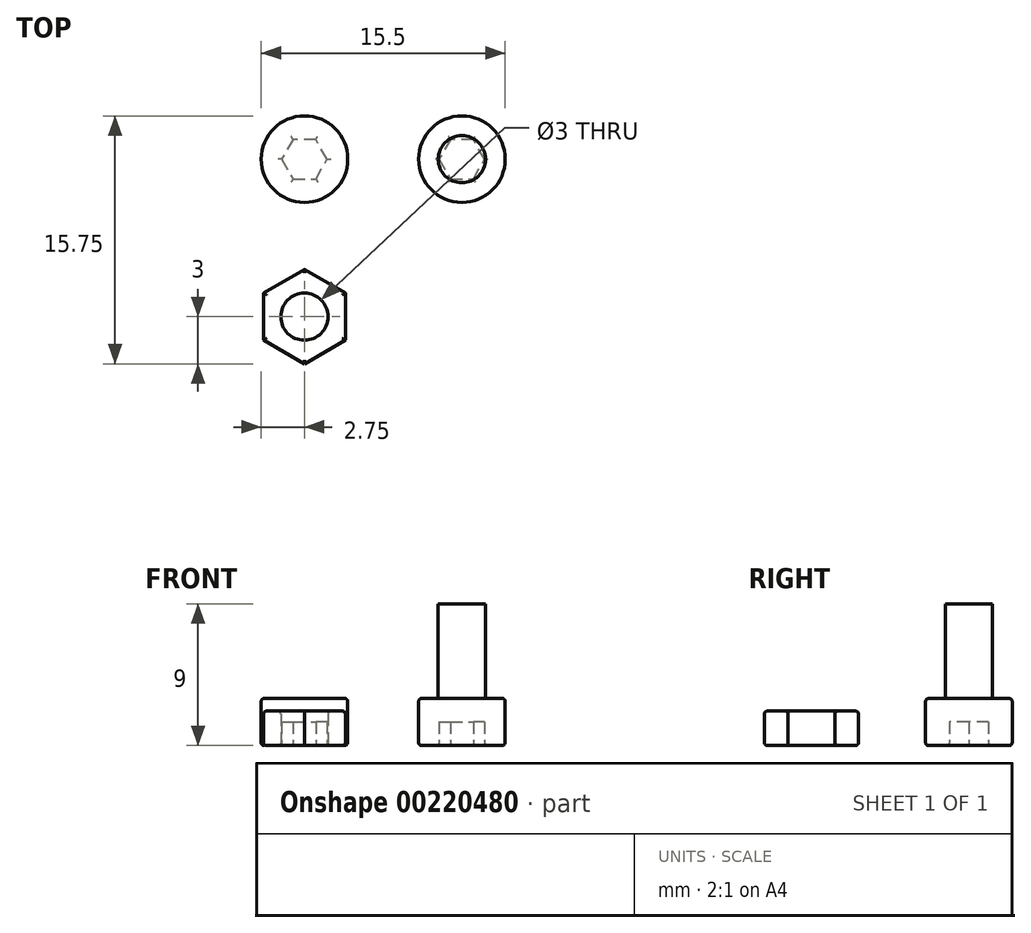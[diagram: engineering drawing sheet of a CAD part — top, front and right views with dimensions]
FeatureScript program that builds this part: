
annotation { "Feature Type Name" : "Feature", "Feature Type Description" : "" }
export const myFeature = defineFeature(function(context is Context, id is Id, definition is map)
    precondition{}
    {
        {
            var Q0;
            Q0=qCreatedBy(makeId("Top.planeOp"),FACE);
            var sketch = newSketch(context, id + "F0", { "sketchPlane" : qUnion([Q0])});
            skCircle(sketch, "E0.cCircle", {"center": v(0, 0) * mm, "radius": 3 * mm, "construction": true});
            skLineSegment(sketch, "E0.0", {"start": v(0, 3) * mm, "end": v(2.6, 1.5) * mm});
            skLineSegment(sketch, "E0.1", {"start": v(2.6, 1.5) * mm, "end": v(2.6, -1.5) * mm});
            skLineSegment(sketch, "E0.2", {"start": v(2.6, -1.5) * mm, "end": v(0, -3) * mm});
            skLineSegment(sketch, "E0.3", {"start": v(0, -3) * mm, "end": v(-2.6, -1.5) * mm});
            skLineSegment(sketch, "E0.4", {"start": v(-2.6, -1.5) * mm, "end": v(-2.6, 1.5) * mm});
            skLineSegment(sketch, "E0.5", {"start": v(-2.6, 1.5) * mm, "end": v(0, 3) * mm});
            skCircle(sketch, "E1", {"center": v(0, 0) * mm, "radius": 1.5 * mm});
            skSolve(sketch);
        }
        {
            var Q0;
            Q0 = qSketchRegion(id + "F0", true);
            extrude(context, id + "F1", {"entities" : qUnion([Q0]), "depth" : 2.2 * mm});
        }
        {
            var Q0;
            Q0=makeQuery(id+"F1.opExtrude","CAP_FACE",FACE,{"disambiguationData":[OSD([sQuery(id+"F0.wireOp",EDGE,"E0.0"),sQuery(id+"F0.wireOp",EDGE,"E0.1"),sQuery(id+"F0.wireOp",EDGE,"E0.2"),sQuery(id+"F0.wireOp",EDGE,"E0.3"),sQuery(id+"F0.wireOp",EDGE,"E0.4"),sQuery(id+"F0.wireOp",EDGE,"E0.5"),sQuery(id+"F0.wireOp",EDGE,"E1")])],"isStart":false});
            var Q1;
            Q1=makeQuery(id+"F1.opExtrude","CAP_FACE",FACE,{"disambiguationData":[OSD([sQuery(id+"F0.wireOp",EDGE,"E0.0"),sQuery(id+"F0.wireOp",EDGE,"E0.1"),sQuery(id+"F0.wireOp",EDGE,"E0.2"),sQuery(id+"F0.wireOp",EDGE,"E0.3"),sQuery(id+"F0.wireOp",EDGE,"E0.4"),sQuery(id+"F0.wireOp",EDGE,"E0.5"),sQuery(id+"F0.wireOp",EDGE,"E1")])],"isStart":true});
            fillet(context, id + "F2", {"entities" : qUnion([Q0, Q1]), "radius" : 0.2 * mm, "tangentPropagation" : true, "allowEdgeOverflow" : false});
        }
        {
            var Q0;
            Q0=makeQuery(id+"F1.opExtrude","SWEPT_BODY",BODY,{"disambiguationData":[OSD([sQuery(id+"F0.wireOp",EDGE,"E0.0"),sQuery(id+"F0.wireOp",EDGE,"E0.1"),sQuery(id+"F0.wireOp",EDGE,"E0.2"),sQuery(id+"F0.wireOp",EDGE,"E0.3"),sQuery(id+"F0.wireOp",EDGE,"E0.4"),sQuery(id+"F0.wireOp",EDGE,"E0.5"),sQuery(id+"F0.wireOp",EDGE,"E1")])]});
            transform(context, id + "F3", {"entities" : qUnion([Q0]), "transformType" : TransformType.TRANSLATION_3D, "dx" : -10 * mm, "dy" : 0 * mm, "dz" : 0 * mm, "makeCopy" : false});
        }
        {
            var Q0;
            Q0=qCreatedBy(makeId("Top.planeOp"),FACE);
            var sketch = newSketch(context, id + "F4", { "sketchPlane" : qUnion([Q0])});
            skCircle(sketch, "E2", {"center": v(0, 0) * mm, "radius": 2.75 * mm});
            skSolve(sketch);
        }
        {
            var Q0;
            Q0 = qSketchRegion(id + "F4", true);
            extrude(context, id + "F5", {"entities" : qUnion([Q0]), "depth" : 3 * mm});
        }
        {
            var Q0;
            Q0=makeQuery(id+"F5.opExtrude","CAP_FACE",FACE,{"disambiguationData":[OSD([sQuery(id+"F4.wireOp",EDGE,"E2")])],"isStart":true});
            var sketch = newSketch(context, id + "F6", { "sketchPlane" : qUnion([Q0])});
            skCircle(sketch, "E3.cCircle", {"center": v(0, 0) * mm, "radius": 1.25 * mm, "construction": true});
            skLineSegment(sketch, "E3.0", {"start": v(-0.72, 1.25) * mm, "end": v(0.72, 1.25) * mm});
            skLineSegment(sketch, "E3.1", {"start": v(0.72, 1.25) * mm, "end": v(1.44, 0) * mm});
            skLineSegment(sketch, "E3.2", {"start": v(1.44, 0) * mm, "end": v(0.72, -1.25) * mm});
            skLineSegment(sketch, "E3.3", {"start": v(0.72, -1.25) * mm, "end": v(-0.72, -1.25) * mm});
            skLineSegment(sketch, "E3.4", {"start": v(-0.72, -1.25) * mm, "end": v(-1.44, 0) * mm});
            skLineSegment(sketch, "E3.5", {"start": v(-1.44, 0) * mm, "end": v(-0.72, 1.25) * mm});
            skPoint(sketch, "E3.0.midPoint", {"position": v(0, 1.25) * mm});
            skSolve(sketch);
        }
        {
            var Q0;
            Q0 = qSketchRegion(id + "F6", true);
            extrude(context, id + "F7", {"entities" : qUnion([Q0]), "operationType" : NewBodyOperationType.REMOVE, "oppositeDirection" : true, "depth" : (3 / 2) * mm});
        }
        {
            var Q0;
            Q0=makeQuery(id+"F5.opExtrude","CAP_FACE",FACE,{"disambiguationData":[OSD([sQuery(id+"F4.wireOp",EDGE,"E2")])],"isStart":true});
            var Q1;
            Q1=makeQuery(id+"F5.opExtrude","CAP_FACE",FACE,{"disambiguationData":[OSD([sQuery(id+"F4.wireOp",EDGE,"E2")])],"isStart":false});
            fillet(context, id + "F8", {"entities" : qUnion([Q0, Q1]), "radius" : 0.2 * mm, "tangentPropagation" : true, "allowEdgeOverflow" : false});
        }
        {
            var Q0;
            Q0=makeQuery(id+"F5.opExtrude","SWEPT_BODY",BODY,{"disambiguationData":[OSD([sQuery(id+"F4.wireOp",EDGE,"E2")])]});
            transform(context, id + "F9", {"entities" : qUnion([Q0]), "transformType" : TransformType.TRANSLATION_3D, "dx" : -10 * mm, "dy" : 10 * mm, "dz" : 0 * mm, "makeCopy" : false});
        }
        {
            var Q0;
            Q0=makeQuery(id+"F5.opExtrude","SWEPT_BODY",BODY,{"disambiguationData":[OSD([sQuery(id+"F4.wireOp",EDGE,"E2")])]});
            transform(context, id + "F10", {"entities" : qUnion([Q0]), "transformType" : TransformType.TRANSLATION_3D, "dx" : 10 * mm, "dy" : 0 * mm, "dz" : 0 * mm, "makeCopy" : true});
        }
        {
            var Q0;
            Q0=makeQuery(id+"F10.opPattern","COPY",FACE,{"derivedFrom":makeQuery(id+"F5.opExtrude","CAP_FACE",FACE,{"disambiguationData":[OSD([sQuery(id+"F4.wireOp",EDGE,"E2")])],"isStart":false}),"instanceName":"1"});
            var sketch = newSketch(context, id + "F11", { "sketchPlane" : qUnion([Q0])});
            skCircle(sketch, "E4", {"center": v(0, 10) * mm, "radius": 1.5 * mm});
            skSolve(sketch);
        }
        {
            var Q0;
            Q0 = qSketchRegion(id + "F11", true);
            extrude(context, id + "F12", {"entities" : qUnion([Q0]), "operationType" : NewBodyOperationType.ADD, "depth" : 6 * mm});
        }
    });
